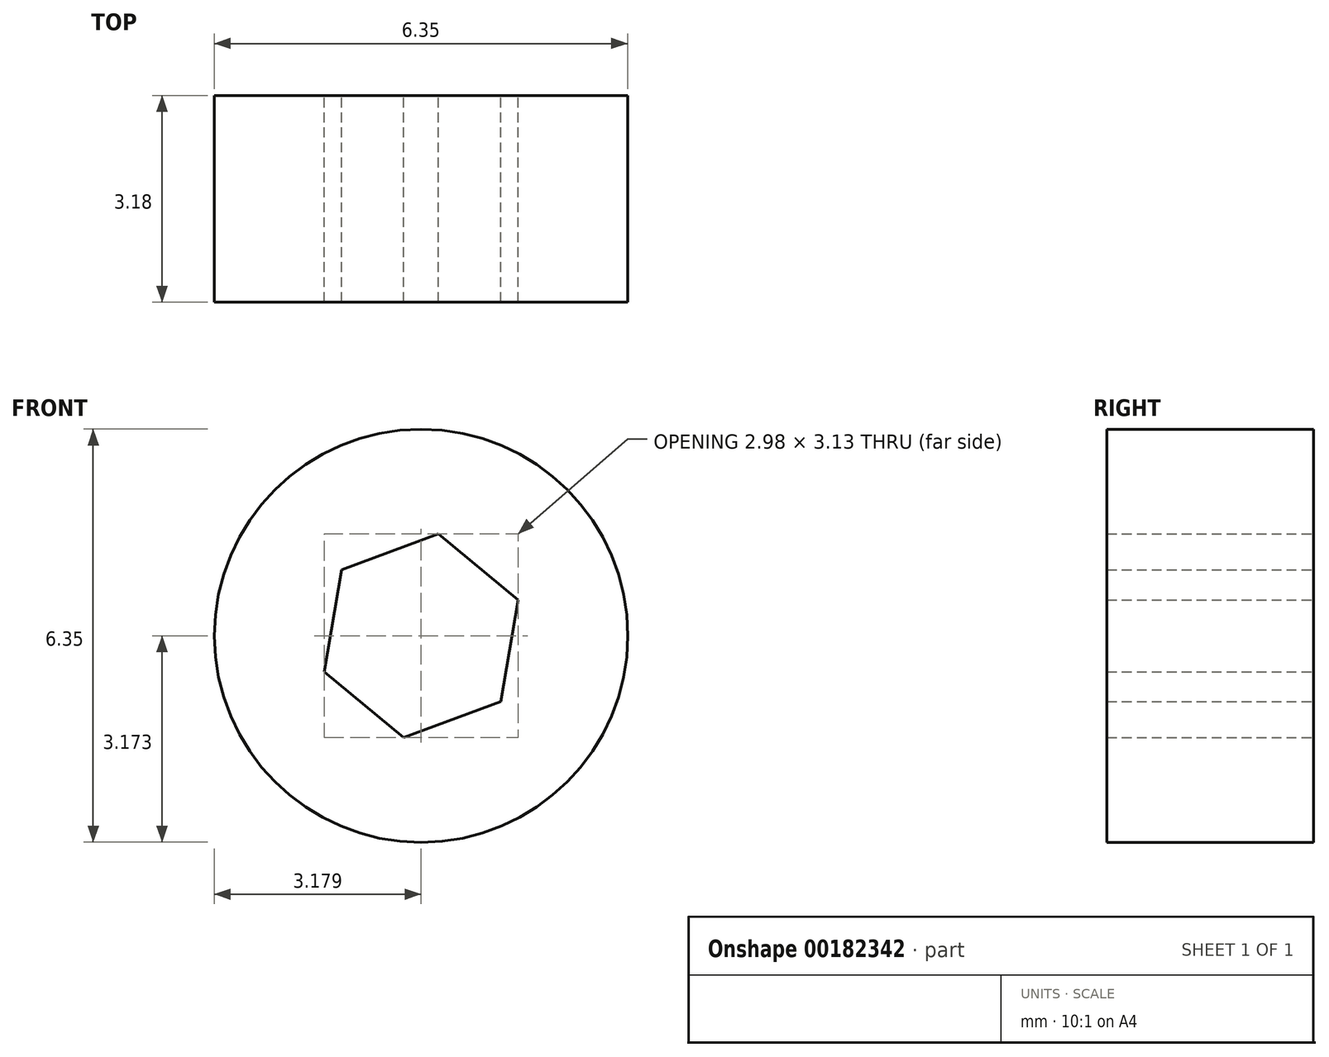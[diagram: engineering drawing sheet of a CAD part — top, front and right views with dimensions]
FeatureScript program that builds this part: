
annotation { "Feature Type Name" : "Feature", "Feature Type Description" : "" }
export const myFeature = defineFeature(function(context is Context, id is Id, definition is map)
    precondition{}
    {
        {
            var Q0;
            Q0=qCreatedBy(makeId("Front.planeOp"),FACE);
            var sketch = newSketch(context, id + "F0", { "sketchPlane" : qUnion([Q0])});
            skPoint(sketch, "E0", {"position": v(-95.22, 41.55) * mm});
            skLineSegment(sketch, "E1.0", {"start": v(-66.69, 46.78) * mm, "end": v(-68.18, 46.23) * mm});
            skLineSegment(sketch, "E1.1", {"start": v(-68.18, 46.23) * mm, "end": v(-69.4, 47.24) * mm});
            skLineSegment(sketch, "E1.2", {"start": v(-69.4, 47.24) * mm, "end": v(-69.13, 48.8) * mm});
            skLineSegment(sketch, "E1.3", {"start": v(-69.13, 48.8) * mm, "end": v(-67.65, 49.36) * mm});
            skLineSegment(sketch, "E1.4", {"start": v(-67.65, 49.36) * mm, "end": v(-66.42, 48.35) * mm});
            skLineSegment(sketch, "E1.5", {"start": v(-66.42, 48.35) * mm, "end": v(-66.69, 46.78) * mm});
            skCircle(sketch, "E2", {"center": v(-67.91, 47.8) * mm, "radius": 3.18 * mm});
            skSolve(sketch);
        }
        {
            var Q0;
            Q0=makeQuery(id+"F0.imprint","IMPRINT",FACE,{"disambiguationData":[TD([[makeQuery(id+"F0.imprint","IMPRINT",EDGE,{"derivedFrom":sQuery(id+"F0.wireOp",EDGE,"E1.0")}),1.0]])]});
            extrude(context, id + "F1", {"entities" : qUnion([Q0]), "depth" : 3.17 * mm});
        }
    });
